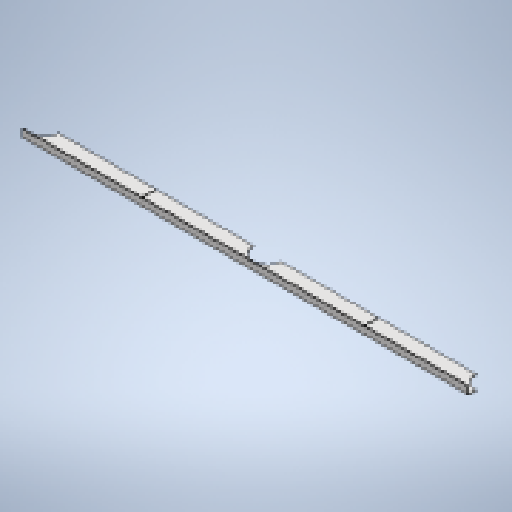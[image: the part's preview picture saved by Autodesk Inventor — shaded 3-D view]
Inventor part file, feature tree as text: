
AUTODESK INVENTOR PART (.ipt)
format: ipt  version: 2025 (Build 290162010, 162A)  size: 357,888 bytes
history: native  units: mm
features: other x5, sheet_metal_op x4, sketch x4, extrude x1
ambient origin geometry x8: Origin, YZ Plane, XZ Plane, XY Plane, X Axis, Y Axis, Z Axis, Center Point
bodies: Solid1 (feature_tree)
feature tree (14):
  sheet_metal_op  "Face1"
  sheet_metal_op  "Flange1"
  extrude  "Extrusion1"  Depth=50.0mm
  other  "Mark1"
  other  "A-Side Definition"
  sketch  "Sketch1"  dims[d0=980.0mm d1=50.0mm]
  other  "Plate1"
  sketch  "Sketch2"  dims[d2=2.0mm]
  other  "Plate2"
  sheet_metal_op  "Bend1"
  sheet_metal_op  "Corner1"
  sketch  "Sketch5"  dims[d3=2.0mm]
  sketch  "Sketch7"  dims[d4=1.0mm d5=4.0mm d6=2.75mm d7=20.0mm d8=90.0deg d9=2.75mm d10=8.0mm d11=2.0mm d12=2.75mm d15=0.0mm d16=0.0mm d30=12.0mm d33=60.0mm d34=2.0mm d35=31.0mm d36=490.0mm]
  other  "Definition1"
